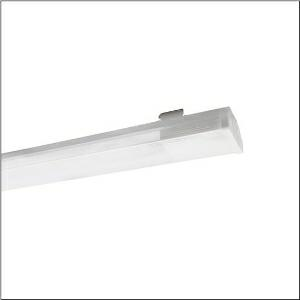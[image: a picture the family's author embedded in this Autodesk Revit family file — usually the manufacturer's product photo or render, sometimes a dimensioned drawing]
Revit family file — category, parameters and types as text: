
# Revit family: modario_31_gen_2_53bm812du4l3d2_8c28
name_source: partatom
category: Lighting Fixtures
units: mm (PartAtom-declared; Revit-internal decimal feet)

## family parameters
Cut with Voids When Loaded = No
Host = Face
Light Source = No
Part Type = Normal
Room Calculation Point = No
Round Connector Dimension = Use Diameter
Shared = No

## types (1)
- --- (1 x LED, 23600 lm, 128.4 W, 4000K)
    Apparent Load = 128 VA
    CIE Flux Codes = 47 80 95 93 100
    Color Rendering = 80
    Color Temperature = 4000K
    Default Elevation = 1800 mm
    Description = Modario 31 Gen.2, luminaire insert, of sheet steel, coil coated, white, length: 2.392mm, width: 81mm, height: 82mm, 8x system unit, system units: 299mm, LED rated luminous flux: 23.600lm, light colour: 840, SDCM (Standard Deviation of Colour Matching)MacAdam ≤ 3 SDCM (initial), control gear: DALI 2, control gear: ECG DALI, with plug, 5-pole, with phase selection, mains connection: 220..240V, AC, 50/60Hz, rated input power: 128W, through-wiring accessed according to module size, primary optical cover: cover, of PMMA, light emission: direct distribution, primary light characteristic: symmetric, protection rating (complete): IP20, protection rating (LED compartment): IP50, insulation class (complete): insulation class I (protective earthing), certification: CE, ENEC, VDE, UKCA, impact resistance: IK03, permissible ambient temperature for indoor applications: -40..+35°C, corresponds to IFS (International Featured Standards) requirements for safety and quality in the food industry, reducing of maximum allowable ambient temperature of 5°C with ceiling mounting, IP40 when using the optional accessory 5TP9018, packaging unit: 1 piece
    Height = 92 mm
    Lamp = 1 x LED
    Lamp Light Flux = 23600 lm
    Lamp Power = 128.4 W
    Lamp count = 1
    Length = 2392 mm
    Luminous efficacy = 184 lm/W
    Manufacturer = Siteco
    ModVariant = No
    Model = 53BM812DU4L3D2
    Mounting Place = Ceiling
    Mounting Type = Pendant
    Number of Poles = 1
    OnlyDefault = Yes
    Power Factor = 1
    Product Name = Modario 31 Gen.2
    Product group = luminaire insert | ceiling pendant
    ProductGroupID = 901
    Protection Class = Protection class I
    Protection Degree = IP 20
    RLX_Detail_Level = 1
    RLX_Emergency_Light_Flux = 0 lm
    RLX_Emergency_Type = 0
    RLX_Emergency_Type_DB = No
    RlxData = <blob elided: 38449 chars, md5=91c4dd6a>
    Socket = socket
    Standby Power = 0 W
    System Light Flux = 23600 lm
    System Power = 128 W
    Type Comments = factory setting: luminous flux: 100 % | dim-lin: 254 | 594 mA
    Type Image = l_1341883.jpg
    URL = http://relux.com
    VarID = @adj_050893
    Voltage = 0 V
    Weight = 0.00 kg
    Width = 81 mm

## geometry (parser evidence)
native form markers: Blend x4, Sweep x12
no freeform markers — native parametric forms only
